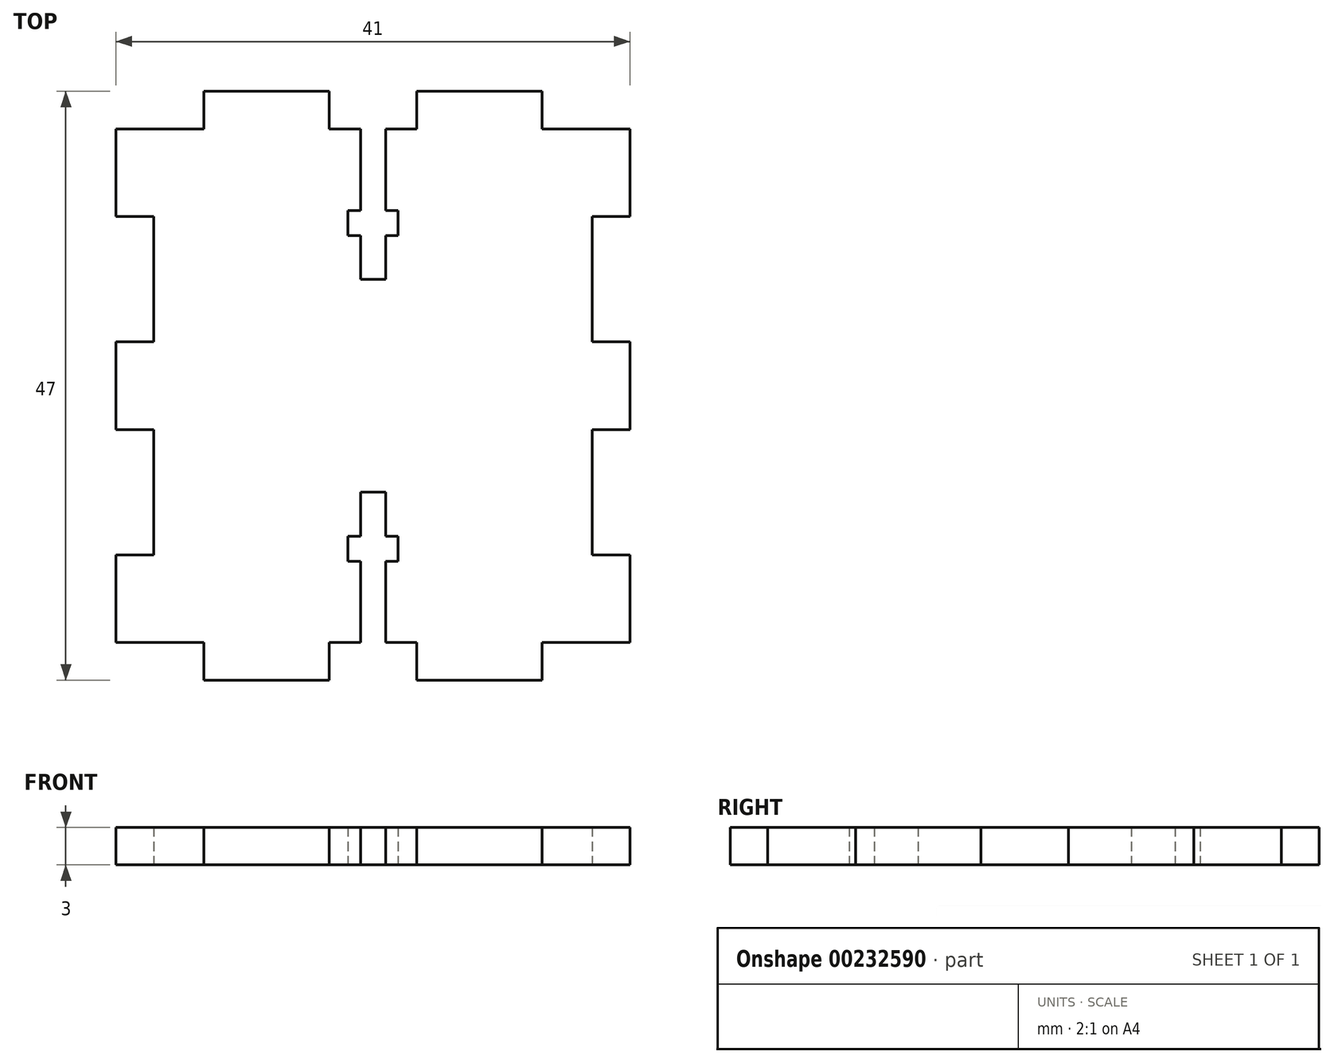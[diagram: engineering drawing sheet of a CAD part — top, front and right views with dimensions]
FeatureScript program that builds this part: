
annotation { "Feature Type Name" : "Feature", "Feature Type Description" : "" }
export const myFeature = defineFeature(function(context is Context, id is Id, definition is map)
    precondition{}
    {
        {
            var Q0;
            Q0=qCreatedBy(makeId("Top.planeOp"),FACE);
            var sketch = newSketch(context, id + "F0", { "sketchPlane" : qUnion([Q0])});
            skLineSegment(sketch, "E0.bottom", {"start": v(-63.35, 28.08) * mm, "end": v(-56.35, 28.08) * mm});
            skLineSegment(sketch, "E0.top", {"start": v(-63.35, -12.92) * mm, "end": v(-56.35, -12.92) * mm});
            skLineSegment(sketch, "E0.left", {"start": v(-63.35, 28.08) * mm, "end": v(-63.35, 21.08) * mm});
            skLineSegment(sketch, "E0.right", {"start": v(-22.35, 28.08) * mm, "end": v(-22.35, 21.08) * mm});
            skLineSegment(sketch, "E1", {"start": v(-63.35, 21.08) * mm, "end": v(-60.35, 21.08) * mm});
            skLineSegment(sketch, "E2", {"start": v(-60.35, 21.08) * mm, "end": v(-60.35, 11.08) * mm});
            skLineSegment(sketch, "E3", {"start": v(-60.35, 11.08) * mm, "end": v(-63.35, 11.08) * mm});
            skLineSegment(sketch, "E4", {"start": v(-63.35, 11.08) * mm, "end": v(-63.35, 4.08) * mm});
            skLineSegment(sketch, "E5", {"start": v(-63.35, 4.08) * mm, "end": v(-60.35, 4.08) * mm});
            skLineSegment(sketch, "E6", {"start": v(-60.35, 4.08) * mm, "end": v(-60.35, -5.92) * mm});
            skLineSegment(sketch, "E7", {"start": v(-60.35, -5.92) * mm, "end": v(-63.35, -5.92) * mm});
            skLineSegment(sketch, "E8", {"start": v(-56.35, 28.08) * mm, "end": v(-56.35, 31.08) * mm});
            skLineSegment(sketch, "E9", {"start": v(-56.35, 31.08) * mm, "end": v(-46.35, 31.08) * mm});
            skLineSegment(sketch, "E10", {"start": v(-46.35, 31.08) * mm, "end": v(-46.35, 28.08) * mm});
            skLineSegment(sketch, "E11", {"start": v(-39.35, 28.08) * mm, "end": v(-39.35, 31.08) * mm});
            skLineSegment(sketch, "E12", {"start": v(-39.35, 31.08) * mm, "end": v(-29.35, 31.08) * mm});
            skLineSegment(sketch, "E13", {"start": v(-29.35, 31.08) * mm, "end": v(-29.35, 28.08) * mm});
            skLineSegment(sketch, "E14.MirrorCS", {"start": v(-56.35, -12.92) * mm, "end": v(-56.35, -15.92) * mm});
            skLineSegment(sketch, "E15.MirrorCS", {"start": v(-56.35, -15.92) * mm, "end": v(-46.35, -15.92) * mm});
            skLineSegment(sketch, "E16.MirrorCS", {"start": v(-46.35, -15.92) * mm, "end": v(-46.35, -12.92) * mm});
            skLineSegment(sketch, "E17.MirrorCS", {"start": v(-39.35, -12.92) * mm, "end": v(-39.35, -15.92) * mm});
            skLineSegment(sketch, "E18.MirrorCS", {"start": v(-39.35, -15.92) * mm, "end": v(-29.35, -15.92) * mm});
            skLineSegment(sketch, "E19.MirrorCS", {"start": v(-29.35, -15.92) * mm, "end": v(-29.35, -12.92) * mm});
            skLineSegment(sketch, "E20.MirrorCS", {"start": v(-22.35, 21.08) * mm, "end": v(-25.35, 21.08) * mm});
            skLineSegment(sketch, "E21.MirrorCS", {"start": v(-25.35, 4.08) * mm, "end": v(-25.35, -5.92) * mm});
            skLineSegment(sketch, "E22.MirrorCS", {"start": v(-25.35, -5.92) * mm, "end": v(-22.35, -5.92) * mm});
            skLineSegment(sketch, "E23.trimOffspring", {"start": v(-29.35, 28.08) * mm, "end": v(-22.35, 28.08) * mm});
            skLineSegment(sketch, "E24", {"start": v(-46.35, 28.08) * mm, "end": v(-43.85, 28.08) * mm});
            skLineSegment(sketch, "E25", {"start": v(-43.85, 28.08) * mm, "end": v(-43.85, 21.58) * mm});
            skLineSegment(sketch, "E26", {"start": v(-43.85, 21.58) * mm, "end": v(-44.85, 21.58) * mm});
            skLineSegment(sketch, "E27", {"start": v(-44.85, 21.58) * mm, "end": v(-44.85, 19.58) * mm});
            skLineSegment(sketch, "E28", {"start": v(-44.85, 19.58) * mm, "end": v(-43.85, 19.58) * mm});
            skLineSegment(sketch, "E29", {"start": v(-43.85, 19.58) * mm, "end": v(-43.85, 16.08) * mm});
            skLineSegment(sketch, "E30", {"start": v(-43.85, 16.08) * mm, "end": v(-41.85, 16.08) * mm});
            skLineSegment(sketch, "E31", {"start": v(-41.85, 16.08) * mm, "end": v(-41.85, 19.58) * mm});
            skLineSegment(sketch, "E32", {"start": v(-41.85, 19.58) * mm, "end": v(-40.85, 19.58) * mm});
            skLineSegment(sketch, "E33", {"start": v(-40.85, 19.58) * mm, "end": v(-40.85, 21.58) * mm});
            skLineSegment(sketch, "E34", {"start": v(-40.85, 21.58) * mm, "end": v(-41.85, 21.58) * mm});
            skLineSegment(sketch, "E35", {"start": v(-41.85, 21.58) * mm, "end": v(-41.85, 28.08) * mm});
            skLineSegment(sketch, "E36", {"start": v(-41.85, 28.08) * mm, "end": v(-39.35, 28.08) * mm});
            skLineSegment(sketch, "E37.MirrorCS", {"start": v(-41.85, -6.42) * mm, "end": v(-41.85, -12.92) * mm});
            skLineSegment(sketch, "E38.MirrorCS", {"start": v(-40.85, -4.42) * mm, "end": v(-40.85, -6.42) * mm});
            skLineSegment(sketch, "E39.MirrorCS", {"start": v(-41.85, -4.42) * mm, "end": v(-40.85, -4.42) * mm});
            skLineSegment(sketch, "E40.MirrorCS", {"start": v(-40.85, -6.42) * mm, "end": v(-41.85, -6.42) * mm});
            skLineSegment(sketch, "E41.MirrorCS", {"start": v(-41.85, -0.92) * mm, "end": v(-41.85, -4.42) * mm});
            skLineSegment(sketch, "E42.MirrorCS", {"start": v(-43.85, -0.92) * mm, "end": v(-41.85, -0.92) * mm});
            skLineSegment(sketch, "E43.MirrorCS", {"start": v(-43.85, -4.42) * mm, "end": v(-43.85, -0.92) * mm});
            skLineSegment(sketch, "E44.MirrorCS", {"start": v(-44.85, -4.42) * mm, "end": v(-43.85, -4.42) * mm});
            skLineSegment(sketch, "E45.MirrorCS", {"start": v(-44.85, -6.42) * mm, "end": v(-44.85, -4.42) * mm});
            skLineSegment(sketch, "E46.MirrorCS", {"start": v(-43.85, -6.42) * mm, "end": v(-44.85, -6.42) * mm});
            skLineSegment(sketch, "E47.MirrorCS", {"start": v(-43.85, -12.92) * mm, "end": v(-43.85, -6.42) * mm});
            skLineSegment(sketch, "E48.trimOffspring", {"start": v(-41.85, -12.92) * mm, "end": v(-39.35, -12.92) * mm});
            skLineSegment(sketch, "E49.trimOffspring", {"start": v(-22.35, -5.92) * mm, "end": v(-22.35, -12.92) * mm});
            skLineSegment(sketch, "E50.trimOffspring", {"start": v(-29.35, -12.92) * mm, "end": v(-22.35, -12.92) * mm});
            skLineSegment(sketch, "E51.trimOffspring", {"start": v(-46.35, -12.92) * mm, "end": v(-43.85, -12.92) * mm});
            skLineSegment(sketch, "E52.trimOffspring", {"start": v(-63.35, -5.92) * mm, "end": v(-63.35, -12.92) * mm});
            skLineSegment(sketch, "E53", {"start": v(-25.35, 4.08) * mm, "end": v(-22.35, 4.08) * mm});
            skLineSegment(sketch, "E54", {"start": v(-25.35, 21.08) * mm, "end": v(-25.35, 11.08) * mm});
            skLineSegment(sketch, "E55", {"start": v(-25.35, 11.08) * mm, "end": v(-22.35, 11.08) * mm});
            skLineSegment(sketch, "E56", {"start": v(-22.35, 11.08) * mm, "end": v(-22.35, 4.08) * mm});
            skSolve(sketch);
        }
        {
            var Q0;
            Q0 = qSketchRegion(id + "F0", true);
            extrude(context, id + "F1", {"entities" : qUnion([Q0]), "depth" : 3 * mm});
        }
    });
